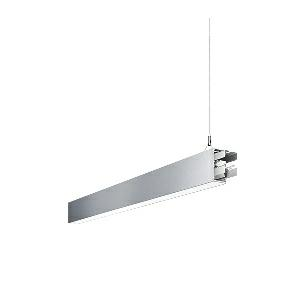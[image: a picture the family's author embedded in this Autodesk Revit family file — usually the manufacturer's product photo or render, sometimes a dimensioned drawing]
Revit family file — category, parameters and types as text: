
# Revit family: idoo_line_-_ilp_2000_840_d_mid_00805684_3006
name_source: partatom
category: Lighting Fixtures
units: mm (PartAtom-declared; Revit-internal decimal feet)

## family parameters
Cut with Voids When Loaded = No
Host = Face
Light Source = No
Part Type = Normal
Room Calculation Point = No
Round Connector Dimension = Use Diameter
Shared = No

## types (1)
- IDOO.line - ILP 2000/840/D MID (1 x LED, 2350 lm, 4000K)
    Apparent Load = 17 VA
    Approval mark = CE
    CIE Flux Codes = 66 91 98 40 100
    Color Rendering = 80-89
    Color Temperature = 4000K
    Control Gear = Electronic ballast
    Default Elevation = 1800 mm
    Description = ILP 2000/840/D|Suspended luminaire|light source: LED|connected load: 220-240 V, 50/60 Hz|Power consumption: approx. 17 W|standby: approx. 0,20|luminous flux: 2350 lm|luminous efficacy: 138 lm/W|light distribution: Direct/indirect|direct ratio: approx. 40 %|colour temperature: Cold white, ca. 4000 K|color rendering index (CRI): >= 80|chromaticity tolerance:  3 SDCM|System of protection: IP 40|technology: Continuously dimmable|luminaire body|material: Sectional aluminium|colour: Silver|lamp cover: Acrylic (PMMA), Clear|mains lead: 1,0 m With free stranded wires|Fastening: Steel cable 0.3 - 0.7 m|glare control: Prism aperture|luminance(L65): <= 2700 cd/m|unified glare rating(4H 8H): <=  16|special features: DALI Load 1x, TouchDIM - dimming via standard switch, Through-wired, up to 18 m on one mains connection, Flicker-free, Suitable as emergency lighting, Mechanical and electrical connection of the individual modules without tools|
    Frequency = 50 Hz
    Height = 110 mm
    Lamp = 1 x LED
    Lamp Light Flux = 2350 lm
    Lamp count = 1
    Length = 842 mm
    Luminous efficacy = 138 lm/W
    Manufacturer = Waldmann
    ModVariant = No
    Model = 00805684
    Mounting Place = Ceiling
    Mounting Type = Pendant
    Number of Poles = 1
    OnlyDefault = Yes
    Power Factor = 1
    Product Name = IDOO.line - ILP 2000/840/D MID
    Product group = Suspended luminaire
    ProductGroupID = 9
    Protection Class = Protection class I
    Protection Degree = IP 40
    RLX_Detail_Level = 1
    RLX_Emergency_Light_Flux = 0 lm
    RLX_Emergency_Type = 0
    RLX_Emergency_Type_DB = No
    RlxData = <blob elided: 19433 chars, md5=2482d960>
    Socket = socket
    Standby Power = 0 W
    System Light Flux = 2350 lm
    System Power = 17 W
    Type Comments = Product without accessories
    Type Image = 113299000-00692561.jpg
    URL = http://relux.com
    VarID = ---
    Voltage = 230 V
    Voltage Range = 220-240 V
    Weight = 0.00 kg
    Width = 60 mm  [stored 0.19685 ft]

note: [stored X ft] marks values corroborated as IEEE doubles in the binary element streams (Revit-internal decimal feet)

## geometry (parser evidence)
native form markers: Blend x4, Sweep x12
no freeform markers — native parametric forms only
